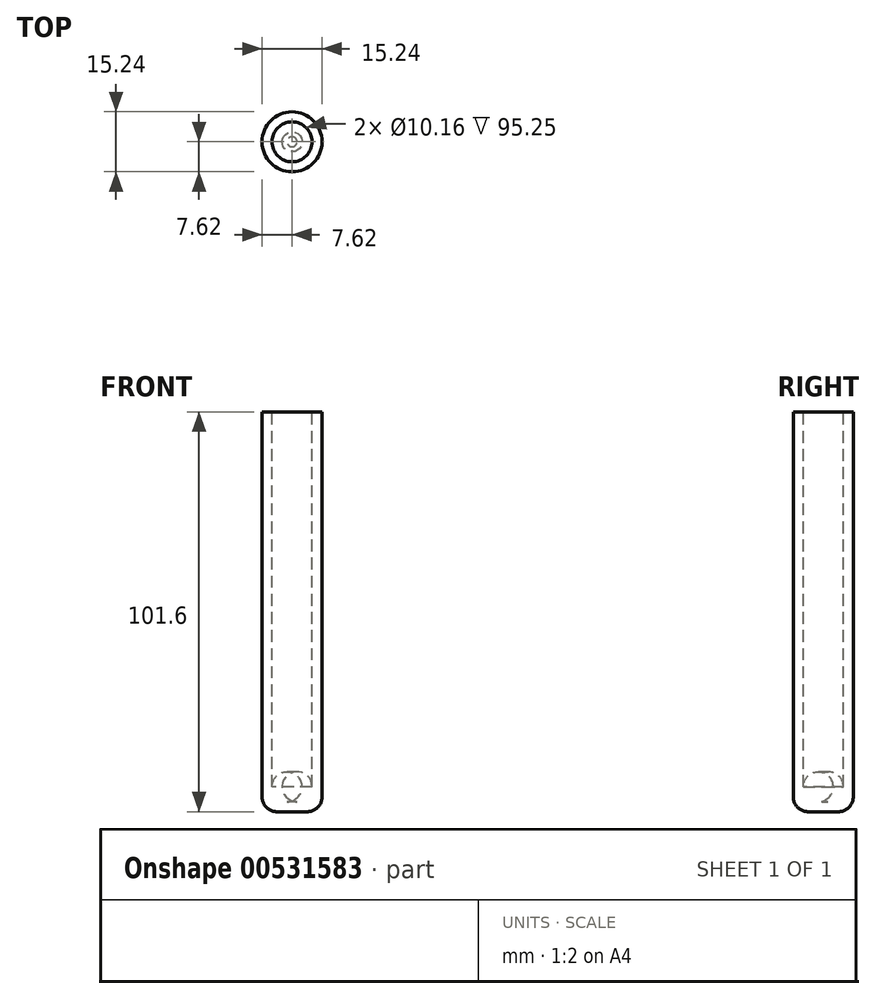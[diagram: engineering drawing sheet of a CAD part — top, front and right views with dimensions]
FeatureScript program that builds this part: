
annotation { "Feature Type Name" : "Feature", "Feature Type Description" : "" }
export const myFeature = defineFeature(function(context is Context, id is Id, definition is map)
    precondition{}
    {
        {
            var Q0;
            Q0=qCreatedBy(makeId("Front.planeOp"),FACE);
            var sketch = newSketch(context, id + "F0", { "sketchPlane" : qUnion([Q0])});
            skLineSegment(sketch, "E0.bottom", {"start": v(0, 0) * mm, "end": v(3.8, 0) * mm});
            skLineSegment(sketch, "E0.top", {"start": v(0, 101.6) * mm, "end": v(7.62, 101.6) * mm});
            skLineSegment(sketch, "E0.left", {"start": v(0, 0) * mm, "end": v(0, 101.6) * mm});
            skLineSegment(sketch, "E0.right", {"start": v(7.62, 3.81) * mm, "end": v(7.62, 101.6) * mm});
            skPoint(sketch, "E1.visualSharp", {"position": v(7.62, 0) * mm});
            skArc(sketch, "E1.filletArc", {"start": v(3.8, 0) * mm, "mid": v(6.5, 1.12) * mm, "end": v(7.62, 3.81) * mm});
            skLineSegment(sketch, "E2.bottom", {"start": v(0, 101.6) * mm, "end": v(5.08, 101.6) * mm});
            skLineSegment(sketch, "E2.top", {"start": v(0, 2.54) * mm, "end": v(1.27, 2.54) * mm});
            skLineSegment(sketch, "E2.left", {"start": v(0, 101.6) * mm, "end": v(0, 2.54) * mm});
            skLineSegment(sketch, "E2.right", {"start": v(5.08, 101.6) * mm, "end": v(5.08, 6.35) * mm});
            skPoint(sketch, "E3.visualSharp", {"position": v(5.08, 2.54) * mm});
            skArc(sketch, "E3.filletArc", {"start": v(1.27, 2.54) * mm, "mid": v(3.96, 3.66) * mm, "end": v(5.08, 6.35) * mm});
            skSolve(sketch);
        }
        {
            var Q0;
            Q0=makeQuery(id+"F0.imprint","IMPRINT",FACE,{"disambiguationData":[TD([[makeQuery(id+"F0.imprint","IMPRINT",EDGE,{"derivedFrom":sQuery(id+"F0.wireOp",EDGE,"E0.bottom")}),1.0]])]});
            var Q1;
            Q1=sQuery(id+"F0.wireOp",EDGE,"E2.left");
            revolve(context, id + "F1", {"entities" : qUnion([Q0]), "axis" : qUnion([Q1]), "revolveType" : RevolveType.FULL});
        }
    });
